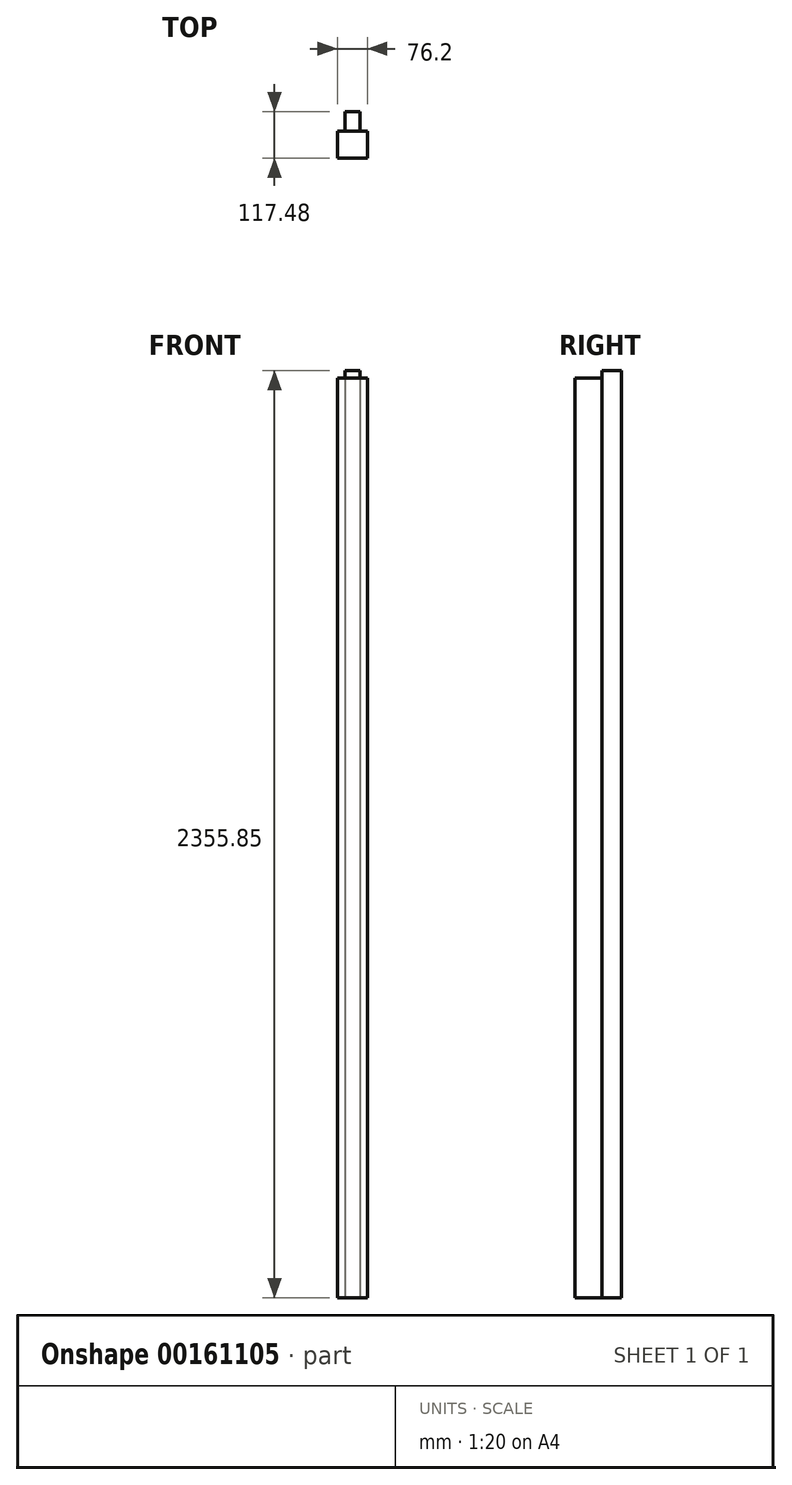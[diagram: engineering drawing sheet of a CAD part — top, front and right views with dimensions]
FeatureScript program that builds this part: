
annotation { "Feature Type Name" : "Feature", "Feature Type Description" : "" }
export const myFeature = defineFeature(function(context is Context, id is Id, definition is map)
    precondition{}
    {
        {
            var Q0;
            Q0=qCreatedBy(makeId("Top.planeOp"),FACE);
            var sketch = newSketch(context, id + "F0", { "sketchPlane" : qUnion([Q0])});
            skLineSegment(sketch, "E0", {"start": v(16.91, 36.7) * mm, "end": v(-21.19, 36.7) * mm});
            skLineSegment(sketch, "E1", {"start": v(-21.19, 36.7) * mm, "end": v(-21.19, -12.52) * mm});
            skLineSegment(sketch, "E2", {"start": v(-21.19, -12.52) * mm, "end": v(-40.24, -12.52) * mm});
            skLineSegment(sketch, "E3", {"start": v(-40.24, -12.52) * mm, "end": v(-40.24, -80.78) * mm});
            skLineSegment(sketch, "E4", {"start": v(-40.24, -80.78) * mm, "end": v(35.96, -80.78) * mm});
            skLineSegment(sketch, "E5", {"start": v(35.96, -80.78) * mm, "end": v(35.96, -12.52) * mm});
            skLineSegment(sketch, "E6", {"start": v(35.96, -12.52) * mm, "end": v(16.91, -12.52) * mm});
            skLineSegment(sketch, "E7", {"start": v(16.91, -12.52) * mm, "end": v(16.91, 36.7) * mm});
            skSolve(sketch);
        }
        {
            var Q0;
            Q0 = qSketchRegion(id + "F0", true);
            extrude(context, id + "F1", {"entities" : qUnion([Q0]), "depth" : 2355.85 * mm});
        }
        {
            var Q0;
            Q0=qCreatedBy(makeId("Right.planeOp"),FACE);
            var sketch = newSketch(context, id + "F2", { "sketchPlane" : qUnion([Q0])});
            skLineSegment(sketch, "E8.0", {"start": v(-80.78, 2355.85) * mm, "end": v(-12.52, 2355.85) * mm});
            skLineSegment(sketch, "E9", {"start": v(-80.78, 2355.85) * mm, "end": v(-80.78, 2336.8) * mm});
            skLineSegment(sketch, "E10", {"start": v(-80.78, 2336.8) * mm, "end": v(-12.52, 2336.8) * mm});
            skLineSegment(sketch, "E11", {"start": v(-12.52, 2336.8) * mm, "end": v(-12.52, 2355.85) * mm});
            skSolve(sketch);
        }
        {
            var Q0;
            Q0 = qSketchRegion(id + "F2", true);
            extrude(context, id + "F3", {"entities" : qUnion([Q0]), "operationType" : NewBodyOperationType.REMOVE, "endBound" : BoundingType.THROUGH_ALL, "oppositeDirection" : true, "depth" : 25.4 * mm, "hasSecondDirection" : true, "secondDirectionBound" : SecondDirectionBoundingType.THROUGH_ALL, "secondDirectionOppositeDirection" : false, "secondDirectionDepth" : 25.4 * mm});
        }
    });
